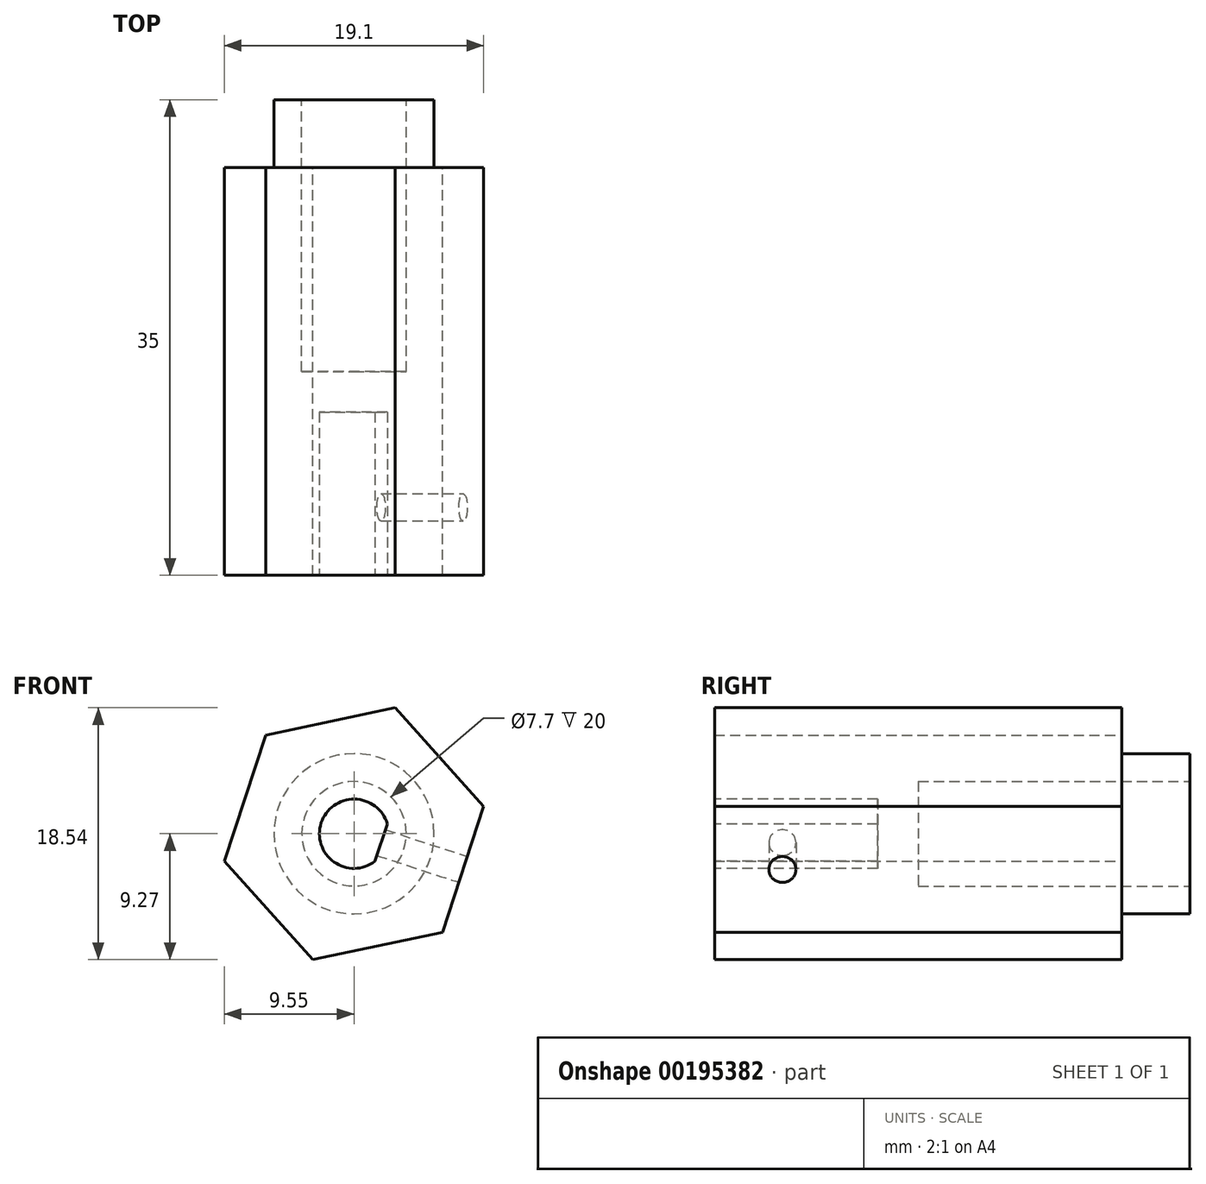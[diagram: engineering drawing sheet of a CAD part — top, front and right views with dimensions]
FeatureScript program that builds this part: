
annotation { "Feature Type Name" : "Feature", "Feature Type Description" : "" }
export const myFeature = defineFeature(function(context is Context, id is Id, definition is map)
    precondition{}
    {
        {
            var Q0;
            Q0=qCreatedBy(makeId("Front.planeOp"),FACE);
            var sketch = newSketch(context, id + "F0", { "sketchPlane" : qUnion([Q0])});
            skCircle(sketch, "E0.cCircle", {"center": v(0, 0) * mm, "radius": 8.45 * mm, "construction": true});
            skLineSegment(sketch, "E0.0", {"start": v(9.55, 2) * mm, "end": v(6.51, -7.27) * mm});
            skLineSegment(sketch, "E0.1", {"start": v(6.51, -7.27) * mm, "end": v(-3.04, -9.27) * mm});
            skLineSegment(sketch, "E0.2", {"start": v(-3.04, -9.27) * mm, "end": v(-9.55, -2) * mm});
            skLineSegment(sketch, "E0.3", {"start": v(-9.55, -2) * mm, "end": v(-6.51, 7.27) * mm});
            skLineSegment(sketch, "E0.4", {"start": v(-6.51, 7.27) * mm, "end": v(3.04, 9.27) * mm});
            skLineSegment(sketch, "E0.5", {"start": v(3.04, 9.27) * mm, "end": v(9.55, 2) * mm});
            skPoint(sketch, "E0.0.midPoint", {"position": v(8.03, -2.63) * mm});
            skSolve(sketch);
        }
        {
            var Q0;
            Q0=makeQuery(id+"F0.imprint","IMPRINT",FACE,{"disambiguationData":[TD([[makeQuery(id+"F0.imprint","IMPRINT",EDGE,{"derivedFrom":sQuery(id+"F0.wireOp",EDGE,"E0.0")}),-1.0]])]});
            extrude(context, id + "F1", {"entities" : qUnion([Q0]), "depth" : 30 * mm});
        }
        {
            var Q0;
            Q0=makeQuery(id+"F1.opExtrude","CAP_FACE",FACE,{"disambiguationData":[OSD([sQuery(id+"F0.wireOp",EDGE,"E0.0"),sQuery(id+"F0.wireOp",EDGE,"E0.1"),sQuery(id+"F0.wireOp",EDGE,"E0.2"),sQuery(id+"F0.wireOp",EDGE,"E0.3"),sQuery(id+"F0.wireOp",EDGE,"E0.4"),sQuery(id+"F0.wireOp",EDGE,"E0.5")])],"isStart":true});
            var sketch = newSketch(context, id + "F2", { "sketchPlane" : qUnion([Q0])});
            skCircle(sketch, "E1", {"center": v(0, 0) * mm, "radius": 5.9 * mm});
            skSolve(sketch);
        }
        {
            var Q0;
            Q0 = qSketchRegion(id + "F2", true);
            extrude(context, id + "F3", {"entities" : qUnion([Q0]), "operationType" : NewBodyOperationType.ADD, "depth" : 5 * mm});
        }
        {
            var Q0;
            Q0=makeQuery(id+"F3.opExtrude","CAP_FACE",FACE,{"disambiguationData":[OSD([sQuery(id+"F2.wireOp",EDGE,"E1")])],"isStart":false});
            var sketch = newSketch(context, id + "F4", { "sketchPlane" : qUnion([Q0])});
            skCircle(sketch, "E2", {"center": v(0, 0) * mm, "radius": 3.85 * mm});
            skSolve(sketch);
        }
        {
            var Q0;
            Q0=makeQuery(id+"F4.imprint","IMPRINT",FACE,{"disambiguationData":[TD([[makeQuery(id+"F4.imprint","IMPRINT",EDGE,{"derivedFrom":sQuery(id+"F4.wireOp",EDGE,"E2")}),1.0]])]});
            extrude(context, id + "F5", {"entities" : qUnion([Q0]), "operationType" : NewBodyOperationType.REMOVE, "oppositeDirection" : true, "depth" : 20 * mm});
        }
        {
            var Q0;
            Q0=makeQuery(id+"F1.opExtrude","CAP_FACE",FACE,{"disambiguationData":[OSD([sQuery(id+"F0.wireOp",EDGE,"E0.0"),sQuery(id+"F0.wireOp",EDGE,"E0.1"),sQuery(id+"F0.wireOp",EDGE,"E0.2"),sQuery(id+"F0.wireOp",EDGE,"E0.3"),sQuery(id+"F0.wireOp",EDGE,"E0.4"),sQuery(id+"F0.wireOp",EDGE,"E0.5")])],"isStart":false});
            var sketch = newSketch(context, id + "F6", { "sketchPlane" : qUnion([Q0])});
            skCircle(sketch, "E3", {"center": v(0, 0) * mm, "radius": 2.55 * mm});
            skSolve(sketch);
        }
        {
            var Q0;
            Q0 = qSketchRegion(id + "F6", true);
            extrude(context, id + "F7", {"entities" : qUnion([Q0]), "operationType" : NewBodyOperationType.REMOVE, "oppositeDirection" : true, "depth" : 12 * mm});
        }
        {
            var Q0;
            Q0=makeQuery(id+"F1.opExtrude","CAP_FACE",FACE,{"disambiguationData":[OSD([sQuery(id+"F0.wireOp",EDGE,"E0.0"),sQuery(id+"F0.wireOp",EDGE,"E0.1"),sQuery(id+"F0.wireOp",EDGE,"E0.2"),sQuery(id+"F0.wireOp",EDGE,"E0.3"),sQuery(id+"F0.wireOp",EDGE,"E0.4"),sQuery(id+"F0.wireOp",EDGE,"E0.5")])],"isStart":false});
            var sketch = newSketch(context, id + "F8", { "sketchPlane" : qUnion([Q0])});
            skLineSegment(sketch, "E4.bottom", {"start": v(1.54, -2.03) * mm, "end": v(2.55, -2.36) * mm});
            skLineSegment(sketch, "E4.top", {"start": v(2.44, 0.72) * mm, "end": v(3.45, 0.4) * mm});
            skLineSegment(sketch, "E4.left", {"start": v(1.54, -2.03) * mm, "end": v(2.44, 0.72) * mm});
            skLineSegment(sketch, "E4.right", {"start": v(2.55, -2.36) * mm, "end": v(3.45, 0.4) * mm});
            skSolve(sketch);
        }
        {
            var Q0;
            {var subQ0=sQuery(id+"F8.wireOp",EDGE,"E4.left");Q0=makeQuery(id+"F8.imprint","IMPRINT",FACE,{"disambiguationData":[TD([[makeQuery(id+"F8.imprint","IMPRINT",EDGE,{"derivedFrom":subQ0}),-1.0]])]});}
            var Q1;
            Q1=makeQuery(id+"F5.boolean.opBoolean","COPY",FACE,{"derivedFrom":makeQuery(id+"F5.opExtrude","CAP_FACE",FACE,{"disambiguationData":[OSD([sQuery(id+"F4.wireOp",EDGE,"E2")])],"isStart":false})});
            extrude(context, id + "F9", {"entities" : qUnion([Q0]), "operationType" : NewBodyOperationType.ADD, "endBound" : BoundingType.UP_TO_SURFACE, "oppositeDirection" : true, "endBoundEntityFace" : qUnion([Q1]), "depth" : 25 * mm});
        }
        {
            var Q0;
            Q0=makeQuery(id+"F1.opExtrude","SWEPT_FACE",FACE,{"disambiguationData":[OSD([sQuery(id+"F0.wireOp",EDGE,"E0.0")])]});
            var sketch = newSketch(context, id + "F10", { "sketchPlane" : qUnion([Q0])});
            skCircle(sketch, "E5", {"center": v(-25, 0) * mm, "radius": 1 * mm});
            skPoint(sketch, "E5.centerSnap0", {"position": v(-30, 0) * mm});
            skSolve(sketch);
        }
        {
            var Q0;
            Q0 = qSketchRegion(id + "F10", true);
            extrude(context, id + "F11", {"entities" : qUnion([Q0]), "operationType" : NewBodyOperationType.REMOVE, "endBound" : BoundingType.UP_TO_NEXT, "oppositeDirection" : true, "depth" : 25 * mm});
        }
    });
